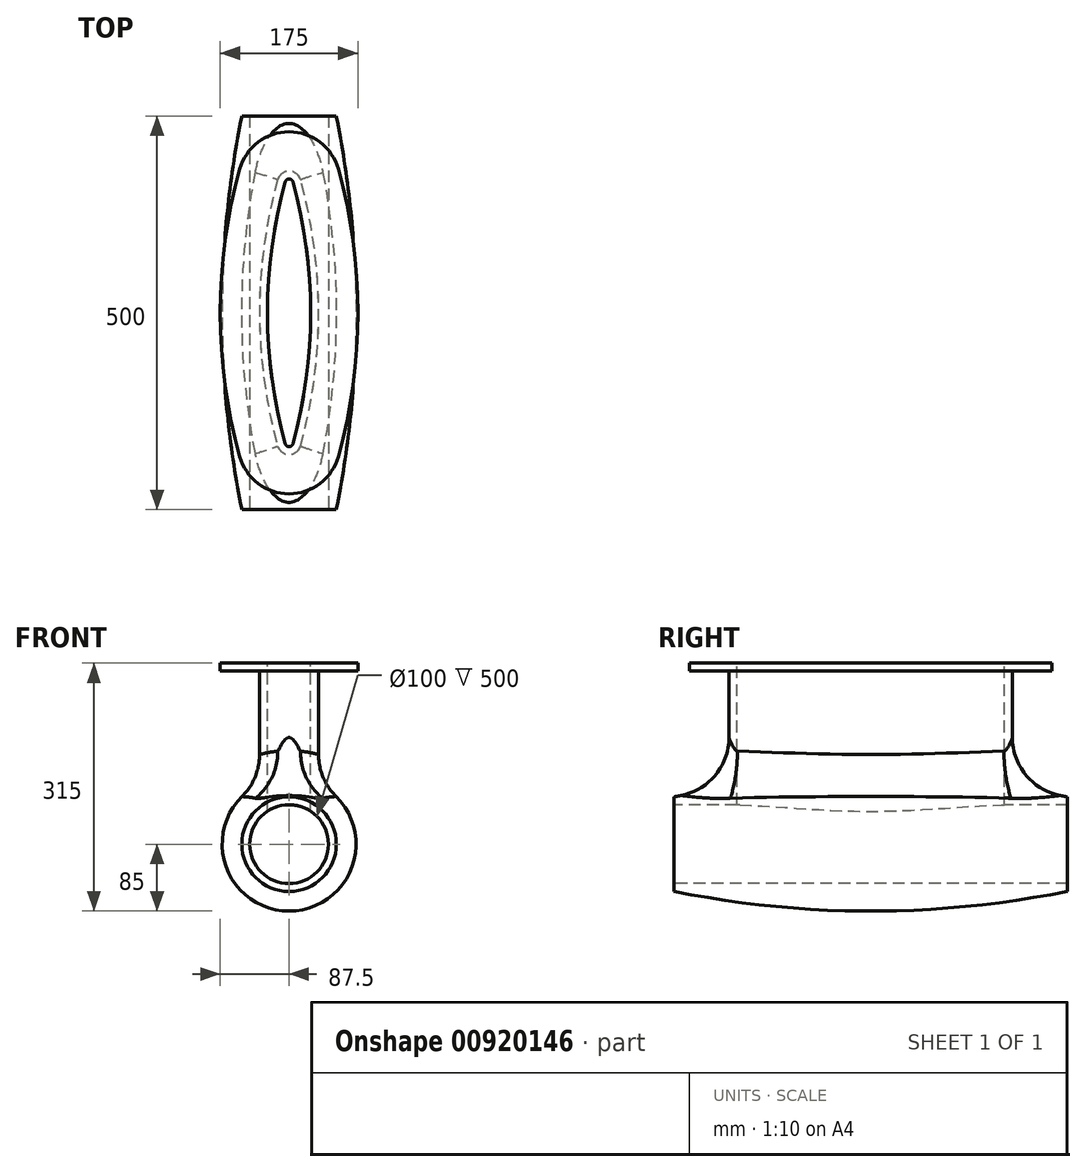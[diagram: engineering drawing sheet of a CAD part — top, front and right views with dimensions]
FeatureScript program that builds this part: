
annotation { "Feature Type Name" : "Feature", "Feature Type Description" : "" }
export const myFeature = defineFeature(function(context is Context, id is Id, definition is map)
    precondition{}
    {
        {
            var Q0;
            Q0=qCreatedBy(makeId("Right.planeOp"),FACE);
            var sketch = newSketch(context, id + "F0", { "sketchPlane" : qUnion([Q0])});
            skArc(sketch, "E0", {"start": v(250, 60) * mm, "mid": v(0, 85) * mm, "end": v(-250, 60) * mm});
            skLineSegment(sketch, "E1", {"start": v(-250, 60) * mm, "end": v(250, 60) * mm, "construction": true});
            skLineSegment(sketch, "E2", {"start": v(0, 60) * mm, "end": v(0, 85) * mm, "construction": true});
            skLineSegment(sketch, "E3", {"start": v(0, 0) * mm, "end": v(-250, 0) * mm, "construction": true});
            skLineSegment(sketch, "E4", {"start": v(-250, 60) * mm, "end": v(-250, 0) * mm});
            skLineSegment(sketch, "E5", {"start": v(250, 60) * mm, "end": v(250, 0) * mm});
            skLineSegment(sketch, "E6", {"start": v(-250, 0) * mm, "end": v(250, 0) * mm});
            skSolve(sketch);
        }
        {
            var Q0;
            Q0 = qSketchRegion(id + "F0", true);
            var Q1;
            Q1=sQuery(id+"F0.wireOp",EDGE,"E6");
            revolve(context, id + "F1", {"surfaceOperationType" : NewSurfaceOperationType.NEW, "entities" : qUnion([Q0]), "axis" : qUnion([Q1]), "revolveType" : RevolveType.FULL});
        }
        {
            var Q0;
            Q0=qCreatedBy(makeId("Top.planeOp"),FACE);
            var sketch = newSketch(context, id + "F2", { "sketchPlane" : qUnion([Q0])});
            skLineSegment(sketch, "E7", {"start": v(0, 0) * mm, "end": v(0, 180) * mm, "construction": true});
            skArc(sketch, "E8", {"start": v(-14.45, 169.02) * mm, "mid": v(0, 180) * mm, "end": v(14.45, 169.02) * mm});
            skArc(sketch, "E9", {"start": v(37.5, 0) * mm, "mid": v(31.71, 85.3) * mm, "end": v(14.45, 169.02) * mm});
            skLineSegment(sketch, "E10", {"start": v(0, 0) * mm, "end": v(37.5, 0) * mm, "construction": true});
            skLineSegment(sketch, "E11", {"start": v(37.5, 0) * mm, "end": v(37.5, -90.19) * mm, "construction": true});
            skLineSegment(sketch, "E12", {"start": v(0, 0) * mm, "end": v(-37.5, 0) * mm, "construction": true});
            skArc(sketch, "E13", {"start": v(-14.45, 169.02) * mm, "mid": v(-31.71, 85.3) * mm, "end": v(-37.5, 0) * mm});
            skLineSegment(sketch, "E14", {"start": v(-37.5, 0) * mm, "end": v(-37.5, -152.75) * mm, "construction": true});
            skArc(sketch, "E15.MirrorCS", {"start": v(-14.45, -169.02) * mm, "mid": v(-31.71, -85.3) * mm, "end": v(-37.5, 0) * mm});
            skArc(sketch, "E16.MirrorCS", {"start": v(-14.45, -169.02) * mm, "mid": v(0, -180) * mm, "end": v(14.45, -169.02) * mm});
            skArc(sketch, "E17.MirrorCS", {"start": v(37.5, 0) * mm, "mid": v(31.71, -85.3) * mm, "end": v(14.45, -169.02) * mm});
            skSolve(sketch);
        }
        {
            var Q0;
            Q0 = qSketchRegion(id + "F2", true);
            extrude(context, id + "F3", {"entities" : qUnion([Q0]), "operationType" : NewBodyOperationType.ADD, "depth" : 230 * mm, "offsetDistance" : 25 * mm});
        }
        {
            var Q0;
            Q0=qCreatedBy(makeId("Front.planeOp"),FACE);
            var sketch = newSketch(context, id + "F4", { "sketchPlane" : qUnion([Q0])});
            skCircle(sketch, "E18", {"center": v(0, 0) * mm, "radius": 50 * mm});
            skSolve(sketch);
        }
        {
            var Q0;
            Q0 = qSketchRegion(id + "F4", true);
            extrude(context, id + "F5", {"entities" : qUnion([Q0]), "operationType" : NewBodyOperationType.REMOVE, "endBound" : BoundingType.SYMMETRIC, "oppositeDirection" : true, "depth" : 786 * mm, "offsetDistance" : 25 * mm});
        }
        {
            var Q0;
            Q0=makeQuery(id+"F3.opExtrude","CAP_FACE",FACE,{"disambiguationData":[OSD([sQuery(id+"F2.wireOp",EDGE,"E8"),sQuery(id+"F2.wireOp",EDGE,"E9"),sQuery(id+"F2.wireOp",EDGE,"E13"),sQuery(id+"F2.wireOp",EDGE,"E15.MirrorCS"),sQuery(id+"F2.wireOp",EDGE,"E16.MirrorCS"),sQuery(id+"F2.wireOp",EDGE,"E17.MirrorCS")])],"isStart":false});
            var sketch = newSketch(context, id + "F6", { "sketchPlane" : qUnion([Q0])});
            skArc(sketch, "E19.0", {"start": v(62.63, 182.4) * mm, "mid": v(0, 230) * mm, "end": v(-62.63, 182.4) * mm});
            skArc(sketch, "E19.1", {"start": v(62.63, -182.4) * mm, "mid": v(87.5, 0) * mm, "end": v(62.63, 182.4) * mm});
            skArc(sketch, "E19.2", {"start": v(-62.63, -182.4) * mm, "mid": v(0, -230) * mm, "end": v(62.63, -182.4) * mm});
            skArc(sketch, "E19.3", {"start": v(-62.63, 182.4) * mm, "mid": v(-87.5, 0) * mm, "end": v(-62.63, -182.4) * mm});
            skSolve(sketch);
        }
        {
            var Q0;
            Q0=makeQuery(id+"F3.opExtrude","CAP_FACE",FACE,{"disambiguationData":[OSD([sQuery(id+"F2.wireOp",EDGE,"E8"),sQuery(id+"F2.wireOp",EDGE,"E9"),sQuery(id+"F2.wireOp",EDGE,"E13"),sQuery(id+"F2.wireOp",EDGE,"E15.MirrorCS"),sQuery(id+"F2.wireOp",EDGE,"E16.MirrorCS"),sQuery(id+"F2.wireOp",EDGE,"E17.MirrorCS")])],"isStart":false});
            var sketch = newSketch(context, id + "F7", { "sketchPlane" : qUnion([Q0])});
            skArc(sketch, "E20.0", {"start": v(4.82, 166.34) * mm, "mid": v(0, 170) * mm, "end": v(-4.82, 166.34) * mm});
            skArc(sketch, "E20.1", {"start": v(4.82, -166.34) * mm, "mid": v(27.5, 0) * mm, "end": v(4.82, 166.34) * mm});
            skArc(sketch, "E20.2", {"start": v(-4.82, -166.34) * mm, "mid": v(0, -170) * mm, "end": v(4.82, -166.34) * mm});
            skArc(sketch, "E20.3", {"start": v(-4.82, 166.34) * mm, "mid": v(-27.5, 0) * mm, "end": v(-4.82, -166.34) * mm});
            skSolve(sketch);
        }
        {
            var Q0;
            Q0=makeQuery(id+"F6.imprint","IMPRINT",FACE,{"disambiguationData":[TD([[makeQuery(id+"F6.imprint","IMPRINT",EDGE,{"derivedFrom":sQuery(id+"F6.wireOp",EDGE,"E19.0")}),1.0]])]});
            extrude(context, id + "F8", {"entities" : qUnion([Q0]), "operationType" : NewBodyOperationType.ADD, "oppositeDirection" : true, "depth" : 10 * mm, "offsetDistance" : 25 * mm});
        }
        {
            var Q0;
            Q0=makeQuery(id+"F7.imprint","IMPRINT",FACE,{"disambiguationData":[TD([[makeQuery(id+"F7.imprint","IMPRINT",EDGE,{"derivedFrom":sQuery(id+"F7.wireOp",EDGE,"E20.0")}),1.0]])]});
            var Q1;
            Q1=makeQuery(id+"F5.boolean.opBoolean","COPY",FACE,{"derivedFrom":makeQuery(id+"F5.opExtrude","SWEPT_FACE",FACE,{"disambiguationData":[OSD([sQuery(id+"F4.wireOp",EDGE,"E18")])]})});
            extrude(context, id + "F9", {"entities" : qUnion([Q0]), "operationType" : NewBodyOperationType.REMOVE, "endBound" : BoundingType.UP_TO_SURFACE, "oppositeDirection" : true, "depth" : 173 * mm, "endBoundEntityFace" : qUnion([Q1]), "offsetDistance" : 25 * mm});
        }
        {
            var Q0;
            Q0=makeQuery(id+"F3.boolean.opBoolean","INTERSECT",EDGE,{"derivedFrom":[makeQuery(id+"F1.opRevolve","SWEPT_FACE",FACE,{"disambiguationData":[OSD([sQuery(id+"F0.wireOp",EDGE,"E0")])]}),makeQuery(id+"F3.opExtrude","SWEPT_FACE",FACE,{"disambiguationData":[OSD([sQuery(id+"F2.wireOp",EDGE,"E13"),sQuery(id+"F2.wireOp",EDGE,"E15.MirrorCS")])]})]});
            var Q1;
            Q1=makeQuery(id+"F8.opExtrude","CAP_EDGE",EDGE,{"disambiguationData":[OSD([sQuery(id+"F2.wireOp",EDGE,"E13"),sQuery(id+"F2.wireOp",EDGE,"E15.MirrorCS")])],"isStart":false});
            fillet(context, id + "F10", {"entities" : qUnion([Q0, Q1]), "tangentPropagation" : true, "radius" : 75 * mm, "defaultsChanged" : true, "vertexSettings" : [], "allowEdgeOverflow" : false});
        }
    });
